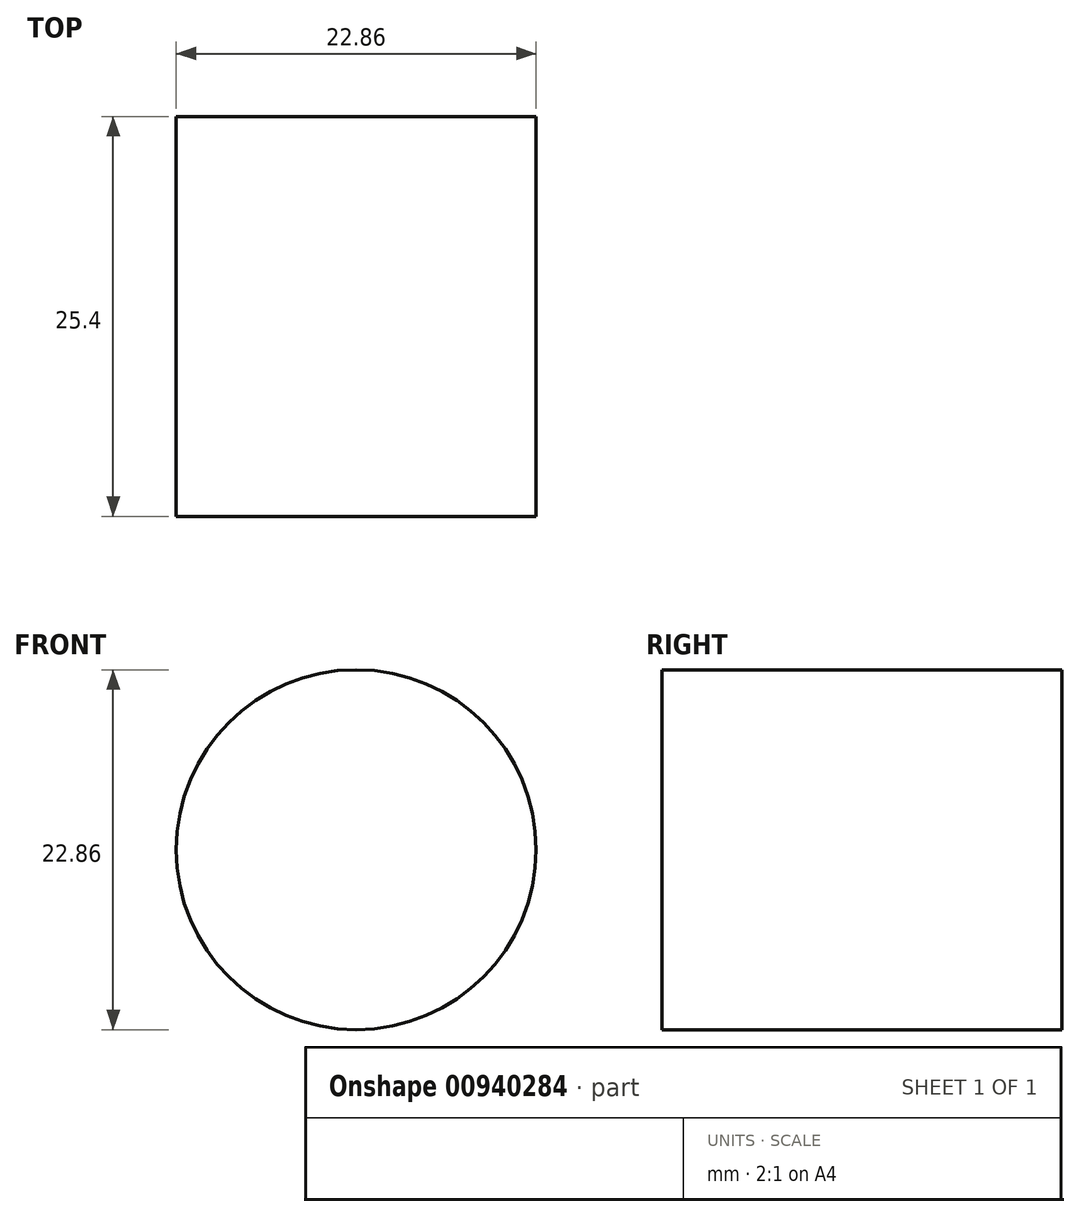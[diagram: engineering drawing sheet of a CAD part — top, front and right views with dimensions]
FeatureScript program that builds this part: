
annotation { "Feature Type Name" : "Feature", "Feature Type Description" : "" }
export const myFeature = defineFeature(function(context is Context, id is Id, definition is map)
    precondition{}
    {
        {
            var Q0;
            Q0=qCreatedBy(makeId("Front.planeOp"),FACE);
            var sketch = newSketch(context, id + "F0", { "sketchPlane" : qUnion([Q0])});
            skCircle(sketch, "E0", {"center": v(0, 0) * mm, "radius": 11.43 * mm});
            skSolve(sketch);
        }
        {
            var Q0;
            Q0=makeQuery(id+"F0.imprint","IMPRINT",FACE,{"disambiguationData":[TD([[makeQuery(id+"F0.imprint","IMPRINT",EDGE,{"derivedFrom":sQuery(id+"F0.wireOp",EDGE,"E0")}),1.0]])]});
            extrude(context, id + "F1", {"entities" : qUnion([Q0]), "depth" : 25.4 * mm, "offsetDistance" : 25.4 * mm});
        }
    });
